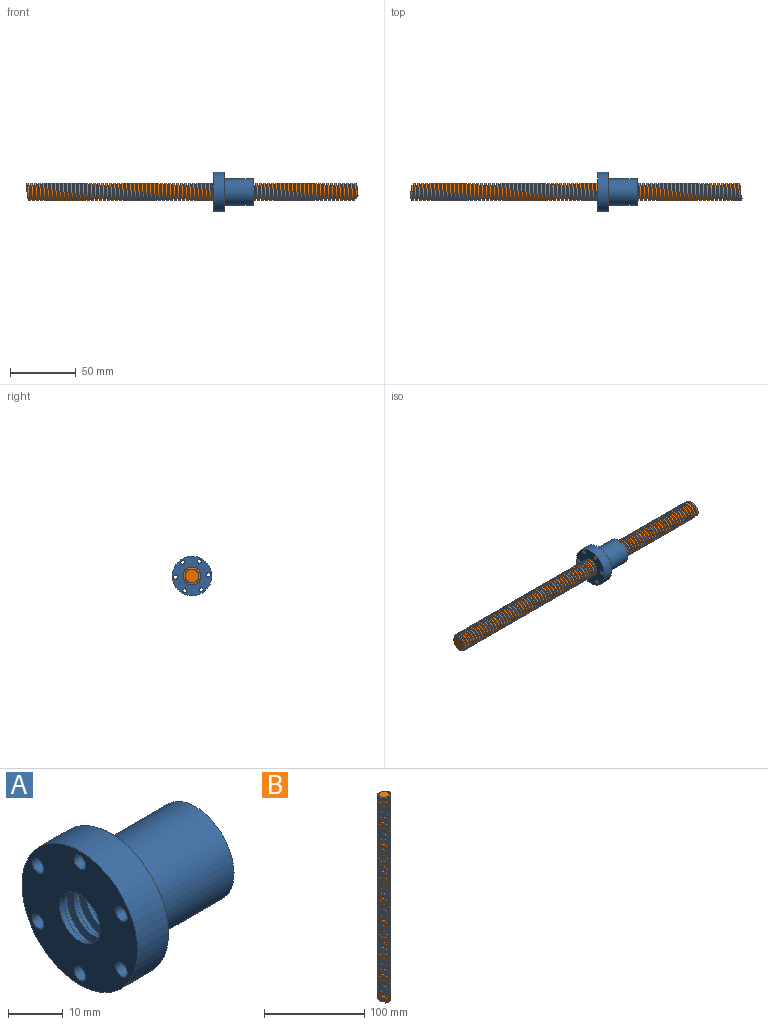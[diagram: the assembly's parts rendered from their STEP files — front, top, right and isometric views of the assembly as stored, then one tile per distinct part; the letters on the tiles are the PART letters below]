
ASSEMBLY  parts=2 mates=1
PART A: 16 faces, bbox 31.1x30.3x30.3 mm
  f0: cylinder r=1.5mm len=8mm, axis (1,0,0), area 75.4mm2, adj f6,f7
  f1: cylinder r=1.5mm len=8mm, axis (1,0,0), area 75.4mm2, adj f6,f7
  f2: cylinder r=1.5mm len=8mm, axis (1,0,0), area 75.4mm2, adj f6,f7
  f3: cylinder r=1.5mm len=8mm, axis (1,0,0), area 75.4mm2, adj f6,f7
  f4: cylinder r=1.5mm len=8mm, axis (1,0,0), area 75.4mm2, adj f6,f7
  f5: cylinder r=15mm len=30mm, axis (-1,0,0), area 754mm2, adj f6,f7
  f6: plane 30x30mm, normal (1,0,0), area 350.3mm2, adj f0,f1,f2,f3,f4,f5,f9,f11
  f7: plane 30x30mm, normal (-1,0,0), area 577.9mm2, adj f0,f1,f2,f3,f4,f5,f8,f11
  f8: cylinder r=5.25mm len=30mm, axis (-1,0,0), area 247.7mm2, adj f7,f10,f12,f13,f15
  f9: cylinder r=10mm len=22mm, axis (-1,0,0), area 1382.3mm2, adj f6,f10
  f10: plane 20.34x20.34mm, normal (1,0,0), area 193.8mm2, adj f8,f9,f13,f14,f15
  f11: cylinder r=1.5mm len=8mm, axis (1,0,0), area 75.4mm2, adj f6,f7
  f12: plane 2.26x1.45mm, normal (0,0,-1), area 2.7mm2, adj f8,f13,f14,f15
  f13: bspline ~30.38x15.48mm, area 559.9mm2, adj f8,f10,f12,f14
  f14: cylinder r=6.7mm len=29.62mm, axis (-1,0,0), area 676.5mm2, adj f10,f12,f13,f15
  f15: bspline ~28.88x15.48mm, area 526.1mm2, adj f8,f10,f12,f14
PART B: 10 faces, bbox 13.4x15.5x252.3 mm
  f0: cylinder r=5.25mm len=250mm, axis (0,0,-1), area 1159.3mm2, adj f1,f2,f4,f5,f6,f8
  f1: plane 10.5x10.5mm, normal (0,0,1), area 86.6mm2, adj f0,f3
  f2: plane 10.5x10.5mm, normal (0,0,-1), area 86.6mm2, adj f0,f7
  f3: cylinder r=5.25mm len=9.8mm, axis (0,0,-1), area 8.6mm2, adj f1,f4,f6
  f4: plane 2.25x1.45mm, normal (0,1,0), area 2.7mm2, adj f0,f3,f6,f8,f9
  f5: plane 2.25x1.26mm, normal (-0.87,0.5,0), area 2.7mm2, adj f0,f6,f7,f8,f9
  f6: bspline ~250.38x15.48mm, area 4713.9mm2, adj f0,f3,f4,f5,f9
  f7: cylinder r=5.25mm len=7.88mm, axis (0,0,-1), area 5.5mm2, adj f2,f5,f8
  f8: bspline ~250.38x15.48mm, area 4717.7mm2, adj f0,f4,f5,f7,f9
  f9: cylinder r=6.7mm len=251.5mm, axis (0,0,-1), area 5263.9mm2, adj f4,f5,f6,f8
PLACE A rot(axis=(-1,0,0),94deg) t=(-133.62,1.17,-4.18)mm
PLACE B rot(axis=(0,-1,0),90deg) t=(-25.05,1.17,-4.18)mm fixed
MATE cylindrical B.f0 <-> A.f8  axis (1,0,0) through (-25.05,1.17,-4.18)mm
